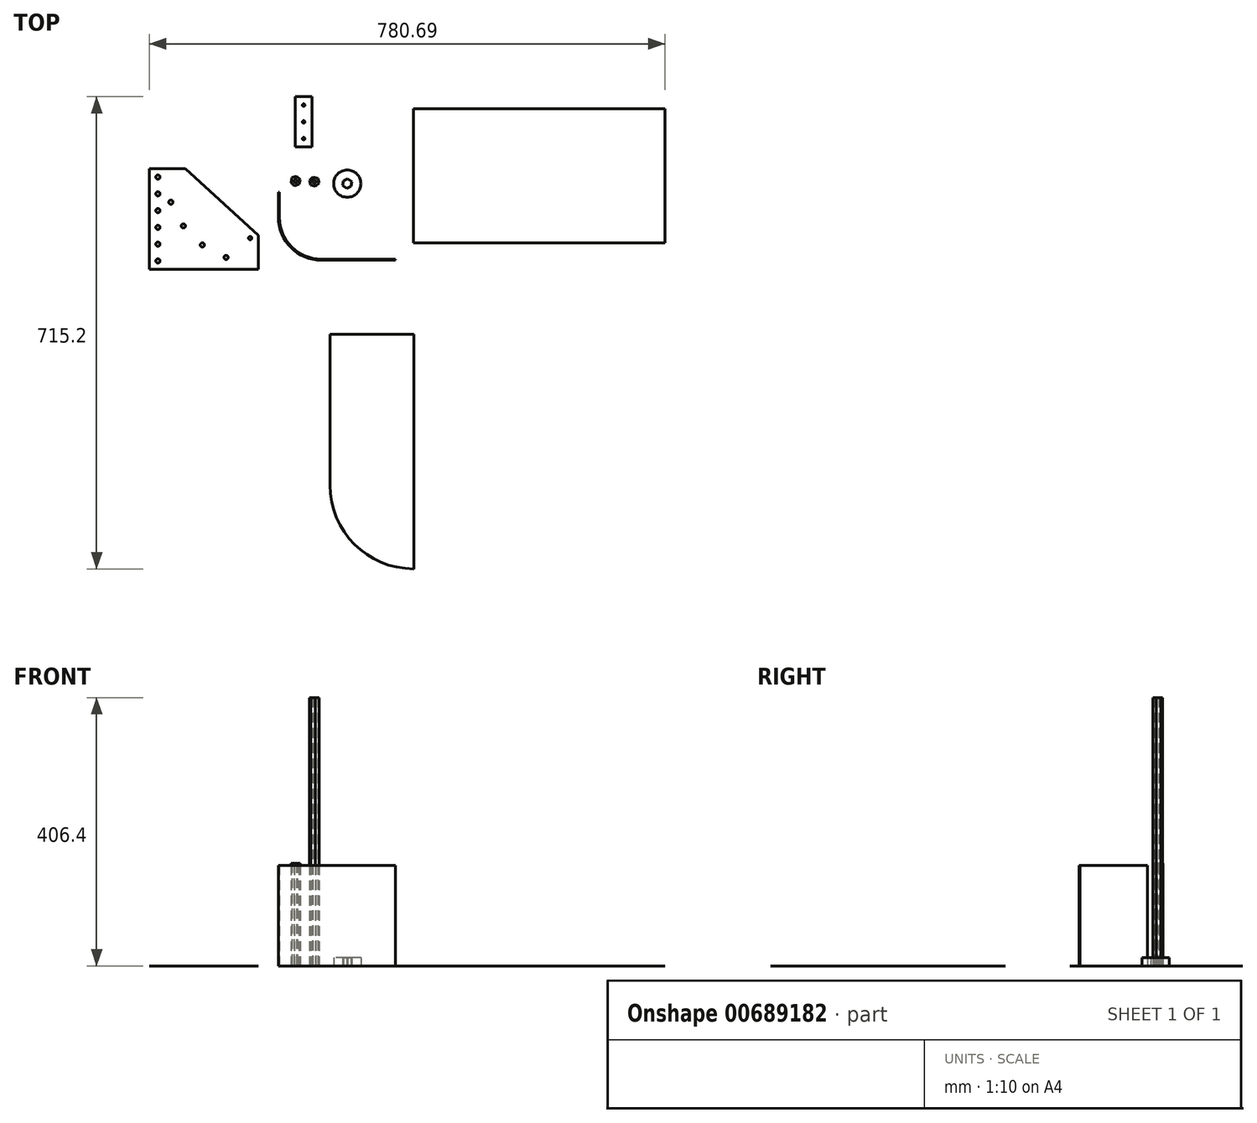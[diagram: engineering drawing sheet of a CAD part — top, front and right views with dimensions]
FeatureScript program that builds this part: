
annotation { "Feature Type Name" : "Feature", "Feature Type Description" : "" }
export const myFeature = defineFeature(function(context is Context, id is Id, definition is map)
    precondition{}
    {
        {
            var Q0;
            Q0=qCreatedBy(makeId("Top.planeOp"),FACE);
            var sketch = newSketch(context, id + "F0", { "sketchPlane" : qUnion([Q0])});
            skLineSegment(sketch, "E0.bottom", {"start": v(-56.65, 74.95) * mm, "end": v(-31.25, 74.95) * mm});
            skLineSegment(sketch, "E0.top", {"start": v(-56.65, -1.25) * mm, "end": v(-31.25, -1.25) * mm});
            skLineSegment(sketch, "E0.left", {"start": v(-56.65, 74.95) * mm, "end": v(-56.65, -1.25) * mm});
            skLineSegment(sketch, "E0.right", {"start": v(-31.25, 74.95) * mm, "end": v(-31.25, -1.25) * mm});
            skPoint(sketch, "E0.middle", {"position": v(-43.95, 36.85) * mm});
            skCircle(sketch, "E1", {"center": v(-43.95, 62.25) * mm, "radius": 1.9 * mm});
            skPoint(sketch, "E1.centerSnap0", {"position": v(-43.95, 74.95) * mm});
            skCircle(sketch, "E2.0.1.0", {"center": v(-43.95, 36.85) * mm, "radius": 1.9 * mm});
            skCircle(sketch, "E2.0.2.0", {"center": v(-43.95, 11.45) * mm, "radius": 1.9 * mm});
            skLineSegment(sketch, "E2.direction1", {"start": v(-43.95, 62.25) * mm, "end": v(-18.55, 62.25) * mm, "construction": true});
            skLineSegment(sketch, "E2.direction2", {"start": v(-43.95, 62.25) * mm, "end": v(-43.95, 36.85) * mm, "construction": true});
            skSolve(sketch);
        }
        {
            var Q0;
            Q0 = qSketchRegion(id + "F0", true);
            extrude(context, id + "F1", {"entities" : qUnion([Q0]), "depth" : 1 / 101.6 * mm, "offsetDistance" : 25.4 * mm});
        }
        {
            var Q0;
            Q0=qCreatedBy(makeId("Top.planeOp"),FACE);
            var sketch = newSketch(context, id + "F2", { "sketchPlane" : qUnion([Q0])});
            skLineSegment(sketch, "E3.bottom", {"start": v(122.27, 56.9) * mm, "end": v(503.27, 56.9) * mm});
            skLineSegment(sketch, "E3.top", {"start": v(122.27, -146.3) * mm, "end": v(503.27, -146.3) * mm});
            skLineSegment(sketch, "E3.left", {"start": v(122.27, 56.9) * mm, "end": v(122.27, -146.3) * mm});
            skLineSegment(sketch, "E3.right", {"start": v(503.27, 56.9) * mm, "end": v(503.27, -146.3) * mm});
            skPoint(sketch, "E3.middle", {"position": v(312.77, -44.7) * mm});
            skSolve(sketch);
        }
        {
            var Q0;
            Q0=makeQuery(id+"F2.imprint","IMPRINT",FACE,{"disambiguationData":[TD([[makeQuery(id+"F2.imprint","IMPRINT",EDGE,{"derivedFrom":sQuery(id+"F2.wireOp",EDGE,"E3.bottom")}),-1.0]])]});
            extrude(context, id + "F3", {"entities" : qUnion([Q0]), "depth" : 1 / 406.4 * mm, "offsetDistance" : 25.4 * mm});
        }
        {
            var Q0;
            Q0=qCreatedBy(makeId("Top.planeOp"),FACE);
            var sketch = newSketch(context, id + "F4", { "sketchPlane" : qUnion([Q0])});
            skArc(sketch, "E4", {"start": v(-244.07, -40.48) * mm, "mid": v(-206.87, -130.28) * mm, "end": v(-117.07, -167.48) * mm, "construction": true});
            skCircle(sketch, "E5", {"center": v(-161.97, -85.38) * mm, "radius": 63.5 * mm, "construction": true});
            skLineSegment(sketch, "E6", {"start": v(-117.07, -40.48) * mm, "end": v(-117.07, -167.48) * mm, "construction": true});
            skLineSegment(sketch, "E7", {"start": v(-117.07, -40.48) * mm, "end": v(-244.07, -40.48) * mm, "construction": true});
            skArc(sketch, "E8.0", {"start": v(-252.53, -40.48) * mm, "mid": v(-212.85, -136.27) * mm, "end": v(-117.07, -175.94) * mm, "construction": true});
            skCircle(sketch, "E9", {"center": v(-245.06, -84.85) * mm, "radius": 6.87 * mm, "construction": true});
            skCircle(sketch, "E10", {"center": v(-161.43, -168.47) * mm, "radius": 6.87 * mm, "construction": true});
            skCircle(sketch, "E11", {"center": v(-197.4, -149.55) * mm, "radius": 6.87 * mm, "construction": true});
            skCircle(sketch, "E12", {"center": v(-226.14, -120.81) * mm, "radius": 6.87 * mm, "construction": true});
            skLineSegment(sketch, "E13", {"start": v(-226.14, -120.81) * mm, "end": v(-245.06, -84.85) * mm, "construction": true});
            skLineSegment(sketch, "E14", {"start": v(-161.43, -168.47) * mm, "end": v(-197.4, -149.55) * mm, "construction": true});
            skLineSegment(sketch, "E15.bottom", {"start": v(-277.42, -34.13) * mm, "end": v(-112.32, -34.13) * mm});
            skLineSegment(sketch, "E15.top", {"start": v(-277.42, -186.53) * mm, "end": v(-112.32, -186.53) * mm});
            skLineSegment(sketch, "E15.left", {"start": v(-277.42, -34.13) * mm, "end": v(-277.42, -186.53) * mm});
            skLineSegment(sketch, "E15.right", {"start": v(-112.32, -34.13) * mm, "end": v(-112.32, -186.53) * mm});
            skPoint(sketch, "E15.middle", {"position": v(-194.87, -110.33) * mm});
            skLineSegment(sketch, "E16.bottom", {"start": v(-609.44, 115.04) * mm, "end": v(-566.06, 115.04) * mm, "construction": true});
            skLineSegment(sketch, "E16.top", {"start": v(-609.44, -333.72) * mm, "end": v(-566.06, -333.72) * mm, "construction": true});
            skLineSegment(sketch, "E16.left", {"start": v(-609.44, 115.04) * mm, "end": v(-609.44, -333.72) * mm, "construction": true});
            skLineSegment(sketch, "E16.right", {"start": v(-566.06, 115.04) * mm, "end": v(-566.06, -333.72) * mm, "construction": true});
            skPoint(sketch, "E16.middle", {"position": v(-587.75, -109.34) * mm});
            skLineSegment(sketch, "E17", {"start": v(-558.11, 47.1) * mm, "end": v(-558.11, -283.16) * mm, "construction": true});
            skLineSegment(sketch, "E18", {"start": v(-558.11, -283.16) * mm, "end": v(-287.65, -283.16) * mm, "construction": true});
            skCircle(sketch, "E19", {"center": v(-438.28, -163.33) * mm, "radius": 119.83 * mm, "construction": true});
            skCircle(sketch, "E20", {"center": v(-161.43, -168.47) * mm, "radius": 3.18 * mm});
            skCircle(sketch, "E21", {"center": v(-197.4, -149.55) * mm, "radius": 3.18 * mm});
            skCircle(sketch, "E22", {"center": v(-245.06, -84.85) * mm, "radius": 3.18 * mm});
            skCircle(sketch, "E23", {"center": v(-226.14, -120.81) * mm, "radius": 3.18 * mm});
            skLineSegment(sketch, "E24", {"start": v(-252.02, -34.13) * mm, "end": v(-252.02, -186.53) * mm, "construction": true});
            skLineSegment(sketch, "E25", {"start": v(-244.07, -40.48) * mm, "end": v(-161.97, -85.38) * mm, "construction": true});
            skLineSegment(sketch, "E26", {"start": v(-161.97, -85.38) * mm, "end": v(-117.07, -167.48) * mm, "construction": true});
            skCircle(sketch, "E27", {"center": v(-264.72, -46.83) * mm, "radius": 3.18 * mm});
            skCircle(sketch, "E28.0.1.0", {"center": v(-264.72, -72.23) * mm, "radius": 3.18 * mm});
            skCircle(sketch, "E28.0.2.0", {"center": v(-264.72, -97.63) * mm, "radius": 3.18 * mm});
            skCircle(sketch, "E28.0.3.0", {"center": v(-264.72, -123.03) * mm, "radius": 3.18 * mm});
            skCircle(sketch, "E28.0.4.0", {"center": v(-264.72, -148.43) * mm, "radius": 3.18 * mm});
            skCircle(sketch, "E28.0.5.0", {"center": v(-264.72, -173.83) * mm, "radius": 3.18 * mm});
            skLineSegment(sketch, "E28.direction1", {"start": v(-264.72, -46.83) * mm, "end": v(-238.96, -46.83) * mm, "construction": true});
            skLineSegment(sketch, "E28.direction2", {"start": v(-264.72, -46.83) * mm, "end": v(-264.72, -72.23) * mm, "construction": true});
            skLineSegment(sketch, "E29", {"start": v(-223.07, -34.13) * mm, "end": v(-112.32, -135.2) * mm});
            skLineSegment(sketch, "E30", {"start": v(-244.07, -40.48) * mm, "end": v(-244.07, -15.44) * mm, "construction": true});
            skLineSegment(sketch, "E31", {"start": v(-117.07, -167.48) * mm, "end": v(-87.75, -167.48) * mm, "construction": true});
            skLineSegment(sketch, "E32", {"start": v(-197.4, -149.55) * mm, "end": v(-226.14, -120.81) * mm, "construction": true});
            skLineSegment(sketch, "E33", {"start": v(-161.43, -168.47) * mm, "end": v(-117.07, -175.94) * mm, "construction": true});
            skLineSegment(sketch, "E34", {"start": v(-252.53, -40.48) * mm, "end": v(-245.06, -84.85) * mm, "construction": true});
            skCircle(sketch, "E35", {"center": v(-125.02, -139.34) * mm, "radius": 2.54 * mm});
            skSolve(sketch);
        }
        {
            var Q0;
            {var subQ4=sQuery(id+"F4.wireOp",EDGE,"E15.top");Q0=makeQuery(id+"F4.imprint","IMPRINT",FACE,{"disambiguationData":[TD([[makeQuery(id+"F4.imprint","IMPRINT",EDGE,{"derivedFrom":subQ4}),1.0]])]});}
            extrude(context, id + "F5", {"entities" : qUnion([Q0]), "depth" : 1 / 101.6 * mm, "offsetDistance" : 25.4 * mm});
        }
        {
            var Q0;
            Q0=qCreatedBy(makeId("Top.planeOp"),FACE);
            var sketch = newSketch(context, id + "F6", { "sketchPlane" : qUnion([Q0])});
            skLineSegment(sketch, "E36.bottom", {"start": v(-4.11, -284.65) * mm, "end": v(122.89, -284.65) * mm});
            skLineSegment(sketch, "E36.top", {"start": v(-4.11, -513.25) * mm, "end": v(122.89, -513.25) * mm, "construction": true});
            skLineSegment(sketch, "E36.left", {"start": v(-4.11, -284.65) * mm, "end": v(-4.11, -513.25) * mm});
            skLineSegment(sketch, "E36.right", {"start": v(122.89, -284.65) * mm, "end": v(122.89, -513.25) * mm});
            skArc(sketch, "E37", {"start": v(-4.11, -513.25) * mm, "mid": v(33.09, -603.06) * mm, "end": v(122.89, -640.25) * mm});
            skLineSegment(sketch, "E38", {"start": v(122.89, -513.25) * mm, "end": v(122.89, -640.25) * mm});
            skSolve(sketch);
        }
        {
            var Q0;
            Q0 = qSketchRegion(id + "F6", true);
            extrude(context, id + "F7", {"entities" : qUnion([Q0]), "depth" : 1 / 203.2 * mm, "offsetDistance" : 25.4 * mm});
        }
        {
            var Q0;
            Q0=qCreatedBy(makeId("Top.planeOp"),FACE);
            var sketch = newSketch(context, id + "F8", { "sketchPlane" : qUnion([Q0])});
            skCircle(sketch, "E39", {"center": v(-56.2, -52.74) * mm, "radius": 2.55 * mm});
            skCircle(sketch, "E40.cCircle", {"center": v(-56.2, -52.74) * mm, "radius": 6.35 * mm, "construction": true});
            skLineSegment(sketch, "E40.0", {"start": v(-50.88, -57.79) * mm, "end": v(-57.9, -59.87) * mm});
            skLineSegment(sketch, "E40.1", {"start": v(-57.9, -59.87) * mm, "end": v(-63.22, -54.82) * mm});
            skLineSegment(sketch, "E40.2", {"start": v(-63.22, -54.82) * mm, "end": v(-61.5, -47.69) * mm});
            skLineSegment(sketch, "E40.3", {"start": v(-61.5, -47.69) * mm, "end": v(-54.48, -45.61) * mm});
            skLineSegment(sketch, "E40.4", {"start": v(-54.48, -45.61) * mm, "end": v(-49.16, -50.66) * mm});
            skLineSegment(sketch, "E40.5", {"start": v(-49.16, -50.66) * mm, "end": v(-50.88, -57.79) * mm});
            skPoint(sketch, "E40.0.midPoint", {"position": v(-54.4, -58.83) * mm});
            skSolve(sketch);
        }
        {
            var Q0;
            Q0=makeQuery(id+"F8.imprint","IMPRINT",FACE,{"disambiguationData":[TD([[makeQuery(id+"F8.imprint","IMPRINT",EDGE,{"derivedFrom":sQuery(id+"F8.wireOp",EDGE,"E39")}),-1.0]])]});
            extrude(context, id + "F9", {"entities" : qUnion([Q0]), "depth" : 155.57 * mm, "offsetDistance" : 25.4 * mm});
        }
        {
            var Q0;
            Q0=qCreatedBy(makeId("Top.planeOp"),FACE);
            var sketch = newSketch(context, id + "F10", { "sketchPlane" : qUnion([Q0])});
            skArc(sketch, "E41", {"start": v(-80.6, -107.68) * mm, "mid": v(-62, -152.58) * mm, "end": v(-17.1, -171.18) * mm});
            skArc(sketch, "E42", {"start": v(-82.2, -107.68) * mm, "mid": v(-63.13, -153.7) * mm, "end": v(-17.1, -172.77) * mm});
            skLineSegment(sketch, "E43", {"start": v(-17.1, -172.77) * mm, "end": v(94.83, -172.77) * mm});
            skLineSegment(sketch, "E44", {"start": v(-82.2, -107.68) * mm, "end": v(-82.2, -69.58) * mm});
            skLineSegment(sketch, "E45", {"start": v(-80.6, -107.68) * mm, "end": v(-80.6, -69.58) * mm});
            skLineSegment(sketch, "E46", {"start": v(-80.6, -69.58) * mm, "end": v(-82.2, -69.58) * mm});
            skLineSegment(sketch, "E47", {"start": v(-17.1, -171.18) * mm, "end": v(94.83, -171.18) * mm});
            skLineSegment(sketch, "E48", {"start": v(94.83, -171.18) * mm, "end": v(94.83, -172.77) * mm});
            skSolve(sketch);
        }
        {
            var Q0;
            Q0=makeQuery(id+"F10.imprint","IMPRINT",FACE,{"disambiguationData":[TD([[makeQuery(id+"F10.imprint","IMPRINT",EDGE,{"derivedFrom":sQuery(id+"F10.wireOp",EDGE,"E41")}),-1.0]])]});
            extrude(context, id + "F11", {"entities" : qUnion([Q0]), "depth" : 152.4 * mm, "offsetDistance" : 25.4 * mm});
        }
        {
            var Q0;
            Q0=qCreatedBy(makeId("Top.planeOp"),FACE);
            var sketch = newSketch(context, id + "F12", { "sketchPlane" : qUnion([Q0])});
            skCircle(sketch, "E49", {"center": v(-27.85, -53.78) * mm, "radius": 2.55 * mm});
            skCircle(sketch, "E50.cCircle", {"center": v(-27.85, -53.78) * mm, "radius": 6.35 * mm, "construction": true});
            skLineSegment(sketch, "E50.0", {"start": v(-20.77, -55.68) * mm, "end": v(-25.96, -60.87) * mm});
            skLineSegment(sketch, "E50.1", {"start": v(-25.96, -60.87) * mm, "end": v(-33.04, -58.97) * mm});
            skLineSegment(sketch, "E50.2", {"start": v(-33.04, -58.97) * mm, "end": v(-34.94, -51.89) * mm});
            skLineSegment(sketch, "E50.3", {"start": v(-34.94, -51.89) * mm, "end": v(-29.75, -46.7) * mm});
            skLineSegment(sketch, "E50.4", {"start": v(-29.75, -46.7) * mm, "end": v(-22.67, -48.6) * mm});
            skLineSegment(sketch, "E50.5", {"start": v(-22.67, -48.6) * mm, "end": v(-20.77, -55.68) * mm});
            skPoint(sketch, "E50.0.midPoint", {"position": v(-23.36, -58.28) * mm});
            skSolve(sketch);
        }
        {
            var Q0;
            Q0=makeQuery(id+"F12.imprint","IMPRINT",FACE,{"disambiguationData":[TD([[makeQuery(id+"F12.imprint","IMPRINT",EDGE,{"derivedFrom":sQuery(id+"F12.wireOp",EDGE,"E49")}),-1.0]])]});
            extrude(context, id + "F13", {"entities" : qUnion([Q0]), "depth" : 406.4 * mm, "offsetDistance" : 25.4 * mm});
        }
        {
            var Q0;
            Q0=qCreatedBy(makeId("Top.planeOp"),FACE);
            var sketch = newSketch(context, id + "F14", { "sketchPlane" : qUnion([Q0])});
            skCircle(sketch, "E51", {"center": v(22.1, -56.71) * mm, "radius": 20.64 * mm});
            skCircle(sketch, "E52.cCircle", {"center": v(22.1, -56.71) * mm, "radius": 6.35 * mm, "construction": true});
            skLineSegment(sketch, "E52.0", {"start": v(28, -61.07) * mm, "end": v(21.27, -64) * mm});
            skLineSegment(sketch, "E52.1", {"start": v(21.27, -64) * mm, "end": v(15.38, -59.64) * mm});
            skLineSegment(sketch, "E52.2", {"start": v(15.38, -59.64) * mm, "end": v(16.2, -52.35) * mm});
            skLineSegment(sketch, "E52.3", {"start": v(16.2, -52.35) * mm, "end": v(22.93, -49.43) * mm});
            skLineSegment(sketch, "E52.4", {"start": v(22.93, -49.43) * mm, "end": v(28.83, -53.79) * mm});
            skLineSegment(sketch, "E52.5", {"start": v(28.83, -53.79) * mm, "end": v(28, -61.07) * mm});
            skPoint(sketch, "E52.0.midPoint", {"position": v(24.63, -62.54) * mm});
            skSolve(sketch);
        }
        {
            var Q0;
            Q0=makeQuery(id+"F14.imprint","IMPRINT",FACE,{"disambiguationData":[TD([[makeQuery(id+"F14.imprint","IMPRINT",EDGE,{"derivedFrom":sQuery(id+"F14.wireOp",EDGE,"E51")}),1.0]])]});
            extrude(context, id + "F15", {"entities" : qUnion([Q0]), "depth" : 12.7 * mm, "offsetDistance" : 25.4 * mm});
        }
    });
